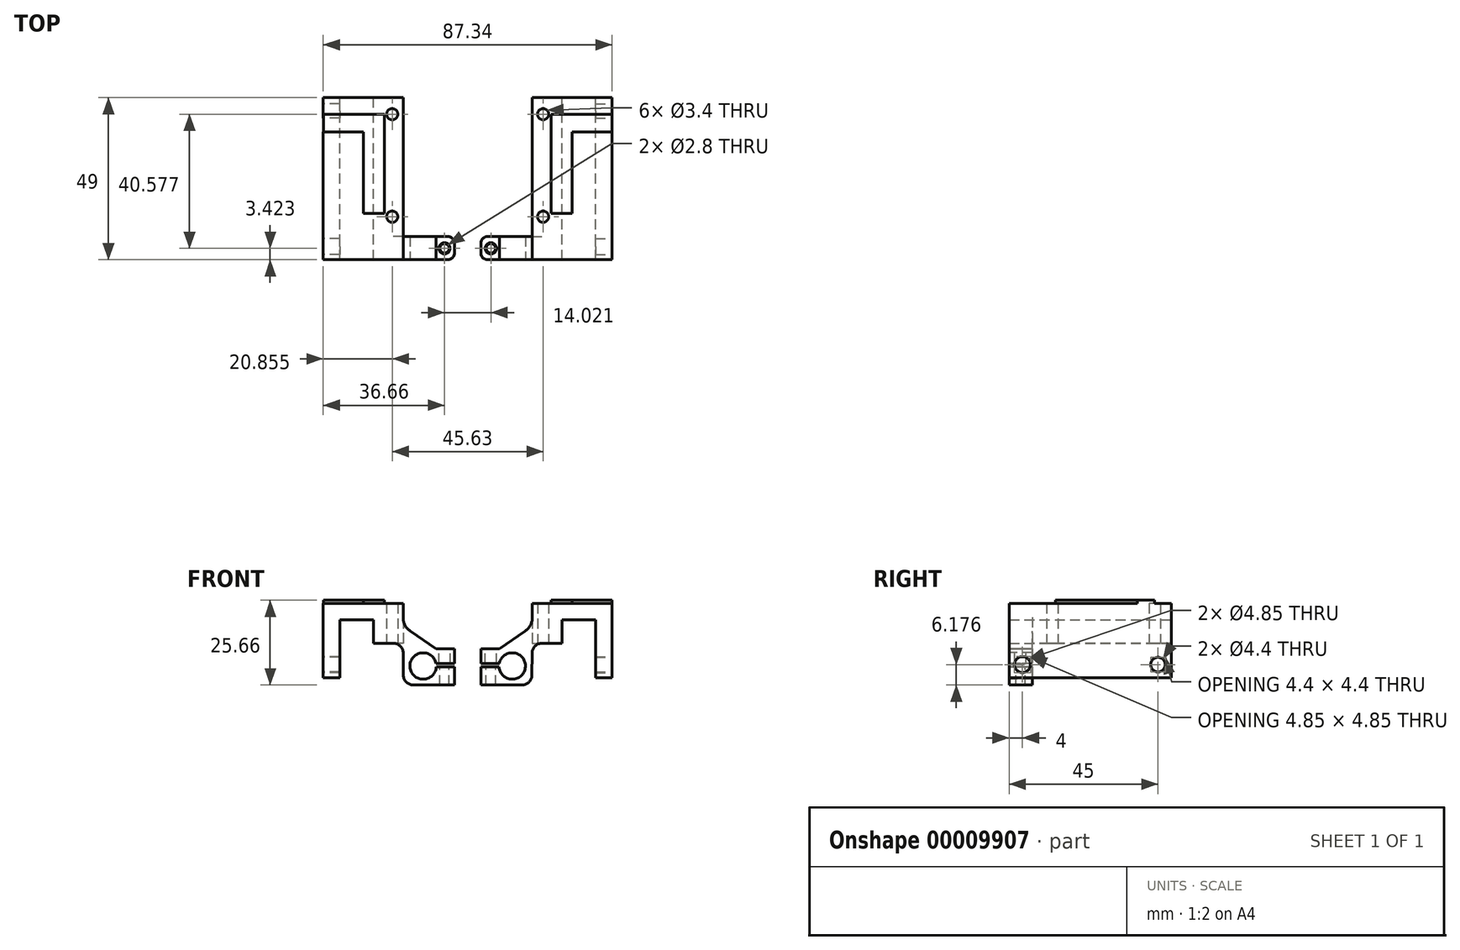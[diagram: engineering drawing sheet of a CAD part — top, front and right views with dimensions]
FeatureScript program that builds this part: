
annotation { "Feature Type Name" : "Feature", "Feature Type Description" : "" }
export const myFeature = defineFeature(function(context is Context, id is Id, definition is map)
    precondition{}
    {
        {
            var Q0;
            Q0=qCreatedBy(makeId("Front.planeOp"),FACE);
            var sketch = newSketch(context, id + "F0", { "sketchPlane" : qUnion([Q0])});
            skLineSegment(sketch, "E0", {"start": v(-18.67, 7.33) * mm, "end": v(-18.67, 29.8) * mm});
            skLineSegment(sketch, "E1", {"start": v(-18.67, 29.8) * mm, "end": v(5.46, 29.8) * mm});
            skLineSegment(sketch, "E2", {"start": v(5.46, 29.8) * mm, "end": v(5.46, 22.94) * mm});
            skLineSegment(sketch, "E3", {"start": v(-3.47, 17.8) * mm, "end": v(-3.47, 24.8) * mm});
            skLineSegment(sketch, "E4", {"start": v(-3.47, 24.8) * mm, "end": v(-13.67, 24.8) * mm});
            skLineSegment(sketch, "E5", {"start": v(-13.67, 24.8) * mm, "end": v(-13.67, 7.33) * mm});
            skLineSegment(sketch, "E6", {"start": v(-13.67, 7.33) * mm, "end": v(-18.67, 7.33) * mm});
            skLineSegment(sketch, "E7", {"start": v(5.46, 22.94) * mm, "end": v(5.46, 17.8) * mm});
            skLineSegment(sketch, "E8", {"start": v(5.46, 17.8) * mm, "end": v(-3.47, 17.8) * mm});
            skLineSegment(sketch, "E9", {"start": v(5.46, 22.94) * mm, "end": v(5.46, 22.94) * mm});
            skLineSegment(sketch, "E10", {"start": v(20.99, 16.14) * mm, "end": v(20.99, 11.7) * mm});
            skLineSegment(sketch, "E11", {"start": v(20.99, 11.7) * mm, "end": v(13.69, 11.7) * mm});
            skLineSegment(sketch, "E12", {"start": v(13.69, 11.7) * mm, "end": v(13.69, 10.67) * mm});
            skLineSegment(sketch, "E13", {"start": v(13.69, 10.67) * mm, "end": v(21.02, 10.67) * mm});
            skLineSegment(sketch, "E14", {"start": v(21.02, 10.67) * mm, "end": v(21.02, 5.15) * mm});
            skLineSegment(sketch, "E15", {"start": v(21.02, 5.15) * mm, "end": v(5.6, 5.15) * mm});
            skLineSegment(sketch, "E16", {"start": v(5.6, 5.15) * mm, "end": v(5.46, 17.8) * mm});
            skLineSegment(sketch, "E17", {"start": v(20.99, 16.14) * mm, "end": v(15.43, 16.14) * mm});
            skLineSegment(sketch, "E18", {"start": v(15.43, 16.14) * mm, "end": v(5.46, 22.94) * mm});
            skSolve(sketch);
        }
        {
            var Q0;
            Q0=makeQuery(id+"F0.imprint","IMPRINT",FACE,{"disambiguationData":[TD([[makeQuery(id+"F0.imprint","IMPRINT",EDGE,{"derivedFrom":sQuery(id+"F0.wireOp",EDGE,"E0")}),-1.0]])]});
            var Q1;
            {var subQ2=sQuery(id+"F0.wireOp",EDGE,"69cbcc5d-e0c3-48db-8baf-3487a8abab7d");Q1=makeQuery(id+"F0.imprint","IMPRINT",FACE,{"disambiguationData":[TD([[makeQuery(id+"F0.imprint","IMPRINT",EDGE,{"derivedFrom":subQ2}),-1.0]])]});}
            var Q2;
            Q2=makeQuery(id+"F0.imprint","IMPRINT",FACE,{"disambiguationData":[TD([[makeQuery(id+"F0.imprint","IMPRINT",EDGE,{"derivedFrom":sQuery(id+"F0.wireOp",EDGE,"E7")}),1.0]])]});
            extrude(context, id + "F1", {"entities" : qUnion([Q0, Q1, Q2]), "depth" : 7 * mm});
        }
        {
            var Q0;
            Q0=makeQuery(id+"F0.imprint","IMPRINT",FACE,{"disambiguationData":[TD([[makeQuery(id+"F0.imprint","IMPRINT",EDGE,{"derivedFrom":sQuery(id+"F0.wireOp",EDGE,"E0")}),-1.0]])]});
            extrude(context, id + "F2", {"entities" : qUnion([Q0]), "operationType" : NewBodyOperationType.ADD, "oppositeDirection" : true, "depth" : 42 * mm});
        }
        {
            var Q0;
            {var subQ0=sQuery(id+"F0.wireOp",EDGE,"E8");Q0=makeQuery(id+"F2.boolean.opBoolean","MERGE",FACE,{"derivedFrom":[makeQuery(id+"F1.opExtrude","SWEPT_FACE",FACE,{"disambiguationData":[OSD([subQ0])]}),makeQuery(id+"F2.opExtrude","SWEPT_FACE",FACE,{"disambiguationData":[OSD([subQ0])]})]});}
            var sketch = newSketch(context, id + "F3", { "sketchPlane" : qUnion([Q0])});
            skCircle(sketch, "E19", {"center": v(2.19, -6) * mm, "radius": 1.7 * mm});
            skCircle(sketch, "E20", {"center": v(2.19, -37) * mm, "radius": 1.7 * mm});
            skCircle(sketch, "E21", {"center": v(17.69, -21.5) * mm, "radius": 11 * mm});
            skSolve(sketch);
        }
        {
            var Q0;
            Q0=qSketchRegion(id+"F3",true);
            extrude(context, id + "F4", {"entities" : qUnion([Q0]), "operationType" : NewBodyOperationType.REMOVE, "endBound" : BoundingType.THROUGH_ALL, "oppositeDirection" : true, "depth" : 25 * mm});
        }
        {
            var Q0;
            Q0=makeQuery(id+"F1.opExtrude","CAP_FACE",FACE,{"disambiguationData":[OSD([sQuery(id+"F0.wireOp",EDGE,"E0"),sQuery(id+"F0.wireOp",EDGE,"E1"),sQuery(id+"F0.wireOp",EDGE,"E2"),sQuery(id+"F0.wireOp",EDGE,"E3"),sQuery(id+"F0.wireOp",EDGE,"E4"),sQuery(id+"F0.wireOp",EDGE,"E5"),sQuery(id+"F0.wireOp",EDGE,"E6"),sQuery(id+"F0.wireOp",EDGE,"E8"),sQuery(id+"F0.wireOp",EDGE,"E9"),sQuery(id+"F0.wireOp",EDGE,"58f11638-63e7-4b32-8aff-a1ba3c53649b"),sQuery(id+"F0.wireOp",EDGE,"E10"),sQuery(id+"F0.wireOp",EDGE,"E11"),sQuery(id+"F0.wireOp",EDGE,"E12"),sQuery(id+"F0.wireOp",EDGE,"E13"),sQuery(id+"F0.wireOp",EDGE,"E14"),sQuery(id+"F0.wireOp",EDGE,"E15"),sQuery(id+"F0.wireOp",EDGE,"E16")])],"isStart":false});
            var sketch = newSketch(context, id + "F5", { "sketchPlane" : qUnion([Q0])});
            skCircle(sketch, "E22", {"center": v(11.53, 10.9) * mm, "radius": 4 * mm});
            skSolve(sketch);
        }
        {
            var Q0;
            Q0=qSketchRegion(id+"F5",true);
            extrude(context, id + "F6", {"entities" : qUnion([Q0]), "operationType" : NewBodyOperationType.REMOVE, "oppositeDirection" : true, "depth" : 10 * mm});
        }
        {
            var Q0;
            Q0=qSketchRegion(id+"F3",true);
            extrude(context, id + "F7", {"entities" : qUnion([Q0]), "operationType" : NewBodyOperationType.REMOVE, "endBound" : BoundingType.THROUGH_ALL, "oppositeDirection" : true, "depth" : 25 * mm});
        }
        {
            var Q0;
            Q0=makeQuery(id+"F1.opExtrude","SWEPT_FACE",FACE,{"disambiguationData":[OSD([sQuery(id+"F0.wireOp",EDGE,"E17")])]});
            var sketch = newSketch(context, id + "F8", { "sketchPlane" : qUnion([Q0])});
            skCircle(sketch, "E23", {"center": v(17.99, -3.58) * mm, "radius": 1.7 * mm});
            skCircle(sketch, "E24", {"center": v(17.99, -3.58) * mm, "radius": 1.4 * mm});
            skSolve(sketch);
        }
        {
            var Q0;
            Q0=makeQuery(id+"F8.imprint","IMPRINT",FACE,{"disambiguationData":[TD([[makeQuery(id+"F8.imprint","IMPRINT",EDGE,{"derivedFrom":sQuery(id+"F8.wireOp",EDGE,"E24")}),1.0]])]});
            extrude(context, id + "F9", {"entities" : qUnion([Q0]), "operationType" : NewBodyOperationType.REMOVE, "endBound" : BoundingType.THROUGH_ALL, "oppositeDirection" : true, "depth" : 25 * mm});
        }
        {
            var Q0;
            Q0=makeQuery(id+"F8.imprint","IMPRINT",FACE,{"disambiguationData":[TD([[makeQuery(id+"F8.imprint","IMPRINT",EDGE,{"derivedFrom":sQuery(id+"F8.wireOp",EDGE,"E23")}),1.0]])]});
            extrude(context, id + "F10", {"entities" : qUnion([Q0]), "operationType" : NewBodyOperationType.REMOVE, "endBound" : BoundingType.UP_TO_NEXT, "oppositeDirection" : true, "depth" : 25 * mm});
        }
        {
            var Q0;
            Q0=makeQuery(id+"F1.opExtrude","SWEPT_EDGE",EDGE,{"disambiguationData":[OSD([sQuery(id+"F0.wireOp",EDGE,"E2"),sQuery(id+"F0.wireOp",EDGE,"E7"),sQuery(id+"F0.wireOp",EDGE,"E18")])]});
            fillet(context, id + "F11", {"entities" : qUnion([Q0]), "radius" : 5 * mm, "tangentPropagation" : true, "allowEdgeOverflow" : false});
        }
        {
            var Q0;
            Q0=makeQuery(id+"F1.opExtrude","SWEPT_EDGE",EDGE,{"disambiguationData":[OSD([sQuery(id+"F0.wireOp",EDGE,"E7"),sQuery(id+"F0.wireOp",EDGE,"E8"),sQuery(id+"F0.wireOp",EDGE,"E16")])]});
            fillet(context, id + "F12", {"entities" : qUnion([Q0]), "radius" : 3 * mm, "tangentPropagation" : true, "allowEdgeOverflow" : false});
        }
        {
            var Q0;
            Q0=makeQuery(id+"F1.opExtrude","SWEPT_EDGE",EDGE,{"disambiguationData":[OSD([sQuery(id+"F0.wireOp",EDGE,"E15"),sQuery(id+"F0.wireOp",EDGE,"E16")])]});
            fillet(context, id + "F13", {"entities" : qUnion([Q0]), "radius" : 3 * mm, "tangentPropagation" : true, "allowEdgeOverflow" : false});
        }
        {
            var Q0;
            Q0=makeQuery(id+"F1.opExtrude","CAP_EDGE",EDGE,{"disambiguationData":[OSD([sQuery(id+"F0.wireOp",EDGE,"E10")])],"isStart":false});
            var Q1;
            Q1=makeQuery(id+"F1.opExtrude","CAP_EDGE",EDGE,{"disambiguationData":[OSD([sQuery(id+"F0.wireOp",EDGE,"E14")])],"isStart":false});
            var Q2;
            Q2=makeQuery(id+"F1.opExtrude","CAP_EDGE",EDGE,{"disambiguationData":[OSD([sQuery(id+"F0.wireOp",EDGE,"E10")])],"isStart":true});
            var Q3;
            Q3=makeQuery(id+"F1.opExtrude","CAP_EDGE",EDGE,{"disambiguationData":[OSD([sQuery(id+"F0.wireOp",EDGE,"E14")])],"isStart":true});
            fillet(context, id + "F14", {"entities" : qUnion([Q0, Q1, Q2, Q3]), "radius" : 2 * mm, "tangentPropagation" : true, "allowEdgeOverflow" : false});
        }
        {
            var Q0;
            {var subQ0=sQuery(id+"F0.wireOp",EDGE,"E0");Q0=makeQuery(id+"F2.boolean.opBoolean","MERGE",FACE,{"derivedFrom":[makeQuery(id+"F1.opExtrude","SWEPT_FACE",FACE,{"disambiguationData":[OSD([subQ0])]}),makeQuery(id+"F2.opExtrude","SWEPT_FACE",FACE,{"disambiguationData":[OSD([subQ0])]})]});}
            var sketch = newSketch(context, id + "F15", { "sketchPlane" : qUnion([Q0])});
            skCircle(sketch, "E25", {"center": v(-38, 11.33) * mm, "radius": 2.2 * mm});
            skCircle(sketch, "E26", {"center": v(3, 11.33) * mm, "radius": 2.43 * mm});
            skSolve(sketch);
        }
        {
            var Q0;
            Q0 = qSketchRegion(id + "F15", true);
            extrude(context, id + "F16", {"entities" : qUnion([Q0]), "operationType" : NewBodyOperationType.REMOVE, "oppositeDirection" : true, "depth" : 6 * mm});
        }
        {
            var Q0;
            {var subQ0=sQuery(id+"F0.wireOp",EDGE,"E1");Q0=makeQuery(id+"F2.boolean.opBoolean","MERGE",FACE,{"derivedFrom":[makeQuery(id+"F1.opExtrude","SWEPT_FACE",FACE,{"disambiguationData":[OSD([subQ0])]}),makeQuery(id+"F2.opExtrude","SWEPT_FACE",FACE,{"disambiguationData":[OSD([subQ0])]})]});}
            var sketch = newSketch(context, id + "F17", { "sketchPlane" : qUnion([Q0])});
            skText(sketch, "E27", { "text": "L", "fontName": "OpenSans-Bold.ttf"});
            const initialGuessF17  = {"E27": [0.0036, 0.03693, -1, 0, 0.0302]};
            skSetInitialGuess(sketch, initialGuessF17);
            skSolve(sketch);
        }
        {
            var Q0;
            Q0 = qSketchRegion(id + "F17", true);
            extrude(context, id + "F18", {"entities" : qUnion([Q0]), "operationType" : NewBodyOperationType.ADD, "depth" : 1 * mm});
        }
        {
            var Q0;
            Q0=makeQuery(id+"F1.opExtrude","SWEPT_BODY",BODY,{"disambiguationData":[OSD([sQuery(id+"F0.wireOp",EDGE,"E0"),sQuery(id+"F0.wireOp",EDGE,"E1"),sQuery(id+"F0.wireOp",EDGE,"E2"),sQuery(id+"F0.wireOp",EDGE,"E3"),sQuery(id+"F0.wireOp",EDGE,"E4"),sQuery(id+"F0.wireOp",EDGE,"E5"),sQuery(id+"F0.wireOp",EDGE,"E6"),sQuery(id+"F0.wireOp",EDGE,"E8"),sQuery(id+"F0.wireOp",EDGE,"E10"),sQuery(id+"F0.wireOp",EDGE,"E11"),sQuery(id+"F0.wireOp",EDGE,"E12"),sQuery(id+"F0.wireOp",EDGE,"E13"),sQuery(id+"F0.wireOp",EDGE,"E14"),sQuery(id+"F0.wireOp",EDGE,"E15"),sQuery(id+"F0.wireOp",EDGE,"E16"),sQuery(id+"F0.wireOp",EDGE,"E17"),sQuery(id+"F0.wireOp",EDGE,"E18")])]});
            var Q1;
            Q1=qCreatedBy(makeId("Right.planeOp"),FACE);
            mirror(context, id + "F19", {"entities" : qUnion([Q0]), "mirrorPlane" : qUnion([Q1])});
        }
        {
            var Q0;
            Q0=makeQuery(id+"F19.opPattern","COPY",BODY,{"derivedFrom":makeQuery(id+"F1.opExtrude","SWEPT_BODY",BODY,{"disambiguationData":[OSD([sQuery(id+"F0.wireOp",EDGE,"E0"),sQuery(id+"F0.wireOp",EDGE,"E1"),sQuery(id+"F0.wireOp",EDGE,"E2"),sQuery(id+"F0.wireOp",EDGE,"E3"),sQuery(id+"F0.wireOp",EDGE,"E4"),sQuery(id+"F0.wireOp",EDGE,"E5"),sQuery(id+"F0.wireOp",EDGE,"E6"),sQuery(id+"F0.wireOp",EDGE,"E8"),sQuery(id+"F0.wireOp",EDGE,"E10"),sQuery(id+"F0.wireOp",EDGE,"E11"),sQuery(id+"F0.wireOp",EDGE,"E12"),sQuery(id+"F0.wireOp",EDGE,"E13"),sQuery(id+"F0.wireOp",EDGE,"E14"),sQuery(id+"F0.wireOp",EDGE,"E15"),sQuery(id+"F0.wireOp",EDGE,"E16"),sQuery(id+"F0.wireOp",EDGE,"E17"),sQuery(id+"F0.wireOp",EDGE,"E18")])]}),"instanceName":"1"});
            transform(context, id + "F20", {"entities" : qUnion([Q0]), "transformType" : TransformType.TRANSLATION_3D, "dx" : 50 * mm, "dy" : 0 * mm, "dz" : 0 * mm, "makeCopy" : false});
        }
    });
